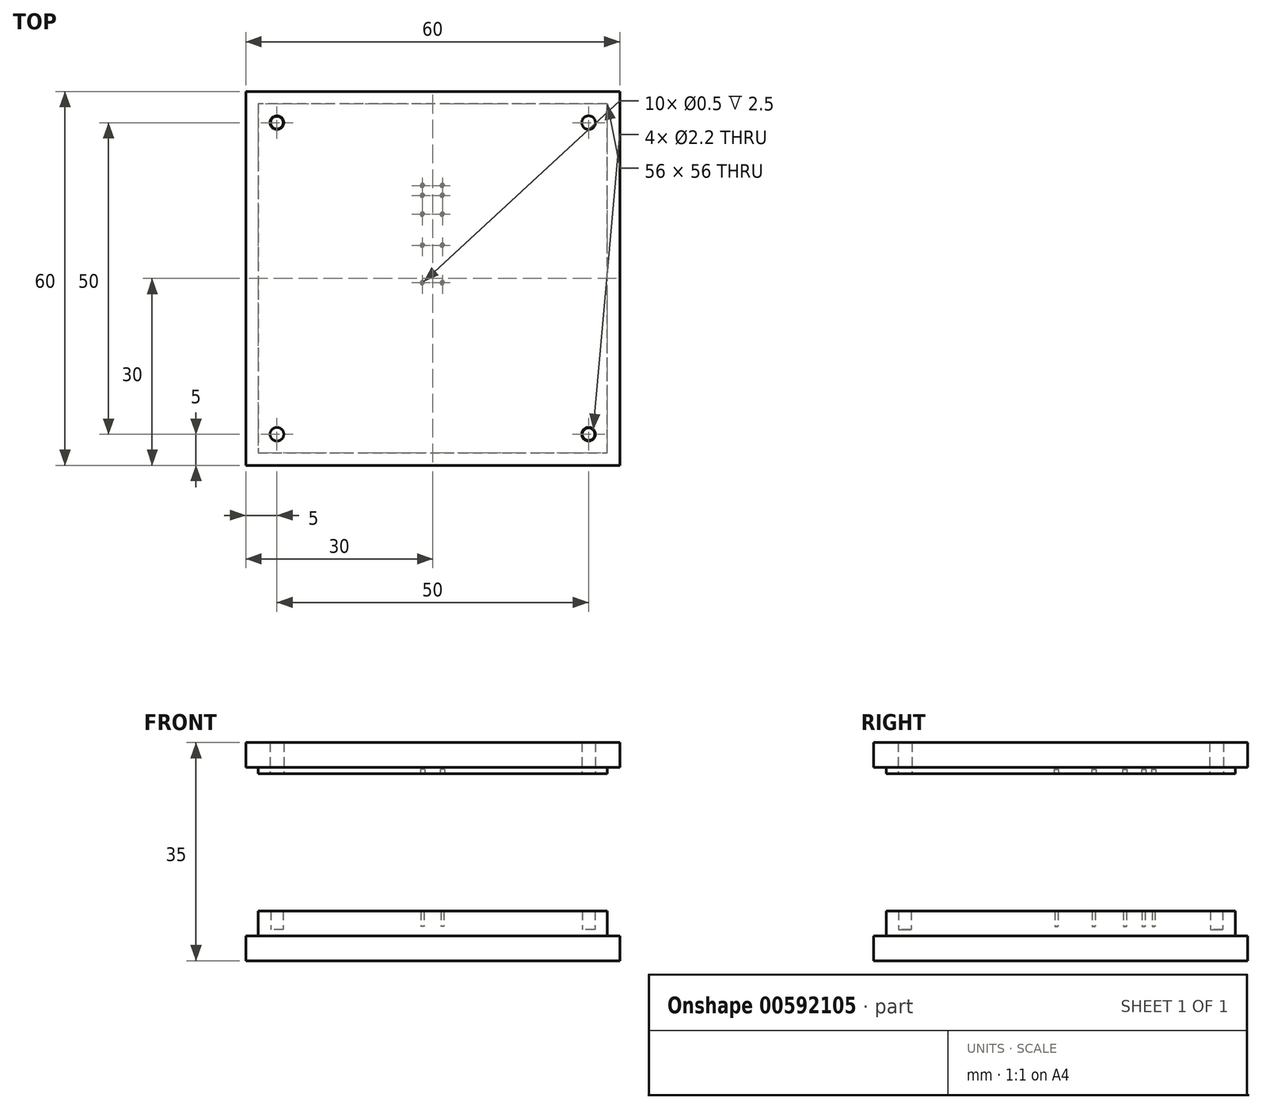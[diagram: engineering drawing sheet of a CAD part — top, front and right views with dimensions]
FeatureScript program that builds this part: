
annotation { "Feature Type Name" : "Feature", "Feature Type Description" : "" }
export const myFeature = defineFeature(function(context is Context, id is Id, definition is map)
    precondition{}
    {
        {
            var Q0;
            Q0=qCreatedBy(makeId("Top.planeOp"),FACE);
            var sketch = newSketch(context, id + "F0", { "sketchPlane" : qUnion([Q0])});
            skCircle(sketch, "E0", {"center": v(-0.48, 13.8) * mm, "radius": 0.03 * mm});
            skCircle(sketch, "E1", {"center": v(-0.48, 13.94) * mm, "radius": 0.03 * mm});
            skCircle(sketch, "E2", {"center": v(-0.48, 14.2) * mm, "radius": 0.03 * mm});
            skCircle(sketch, "E3", {"center": v(-0.13, 13.8) * mm, "radius": 0.05 * mm});
            skCircle(sketch, "E4", {"center": v(-0.13, 14) * mm, "radius": 0.05 * mm});
            skCircle(sketch, "E5", {"center": v(-0.13, 14.3) * mm, "radius": 0.05 * mm});
            skCircle(sketch, "E6", {"center": v(0.4, 13.8) * mm, "radius": 0.1 * mm});
            skCircle(sketch, "E7", {"center": v(0.4, 14.1) * mm, "radius": 0.1 * mm});
            skCircle(sketch, "E8", {"center": v(0.4, 14.5) * mm, "radius": 0.1 * mm});
            skCircle(sketch, "E9", {"center": v(-0.48, 14.5) * mm, "radius": 0.03 * mm});
            skCircle(sketch, "E10", {"center": v(-0.13, 14.6) * mm, "radius": 0.05 * mm});
            skCircle(sketch, "E11", {"center": v(-0.48, 13.8) * mm, "radius": 0.06 * mm});
            skCircle(sketch, "E12", {"center": v(-0.48, 13.94) * mm, "radius": 0.06 * mm});
            skCircle(sketch, "E13", {"center": v(-0.48, 14.2) * mm, "radius": 0.07 * mm});
            skCircle(sketch, "E14", {"center": v(-0.48, 14.5) * mm, "radius": 0.07 * mm});
            skCircle(sketch, "E15", {"center": v(-0.13, 13.8) * mm, "radius": 0.08 * mm});
            skCircle(sketch, "E16", {"center": v(-0.13, 14) * mm, "radius": 0.08 * mm});
            skCircle(sketch, "E17", {"center": v(-0.13, 14.3) * mm, "radius": 0.1 * mm});
            skCircle(sketch, "E18", {"center": v(-0.13, 14.6) * mm, "radius": 0.1 * mm});
            skCircle(sketch, "E19", {"center": v(0.4, 13.8) * mm, "radius": 0.13 * mm});
            skCircle(sketch, "E20", {"center": v(0.4, 14.1) * mm, "radius": 0.13 * mm});
            skCircle(sketch, "E21", {"center": v(0.4, 14.5) * mm, "radius": 0.15 * mm});
            skLineSegment(sketch, "E22", {"start": v(-0.25, 13.36) * mm, "end": v(-0.25, -15.14) * mm});
            skLineSegment(sketch, "E23", {"start": v(-0.21, 13.36) * mm, "end": v(-0.21, -14.64) * mm});
            skLineSegment(sketch, "E24", {"start": v(-0.17, 13.36) * mm, "end": v(-0.17, -14.14) * mm});
            skLineSegment(sketch, "E25", {"start": v(-0.13, 13.36) * mm, "end": v(-0.13, -13.64) * mm});
            skLineSegment(sketch, "E26", {"start": v(-0.09, 13.36) * mm, "end": v(-0.09, -13.14) * mm});
            skLineSegment(sketch, "E27", {"start": v(-0.05, 13.36) * mm, "end": v(-0.05, -12.64) * mm});
            skLineSegment(sketch, "E28", {"start": v(-0.01, 13.36) * mm, "end": v(-0.01, -12.14) * mm});
            skLineSegment(sketch, "E29", {"start": v(0.03, 13.36) * mm, "end": v(0.03, -11.64) * mm});
            skLineSegment(sketch, "E30", {"start": v(0.07, 13.36) * mm, "end": v(0.07, -11.14) * mm});
            skLineSegment(sketch, "E31", {"start": v(0.1, 13.36) * mm, "end": v(0.1, -10.64) * mm});
            skLineSegment(sketch, "E32", {"start": v(0.15, 13.36) * mm, "end": v(0.15, -10.14) * mm});
            skLineSegment(sketch, "E33", {"start": v(2.74, -15.44) * mm, "end": v(2.74, -15.14) * mm});
            skLineSegment(sketch, "E34", {"start": v(2.74, -15.14) * mm, "end": v(-0.26, -15.14) * mm});
            skLineSegment(sketch, "E35", {"start": v(-0.26, -15.14) * mm, "end": v(-0.26, -15.44) * mm});
            skLineSegment(sketch, "E36", {"start": v(-0.26, -15.44) * mm, "end": v(2.74, -15.44) * mm});
            skLineSegment(sketch, "E37", {"start": v(2.74, -14.94) * mm, "end": v(2.74, -14.64) * mm});
            skLineSegment(sketch, "E38", {"start": v(2.74, -14.64) * mm, "end": v(-0.22, -14.64) * mm});
            skLineSegment(sketch, "E39", {"start": v(-0.22, -14.64) * mm, "end": v(-0.22, -14.94) * mm});
            skLineSegment(sketch, "E40", {"start": v(-0.22, -14.94) * mm, "end": v(2.74, -14.94) * mm});
            skLineSegment(sketch, "E41", {"start": v(2.74, -14.44) * mm, "end": v(2.74, -14.14) * mm});
            skLineSegment(sketch, "E42", {"start": v(2.74, -14.14) * mm, "end": v(-0.18, -14.14) * mm});
            skLineSegment(sketch, "E43", {"start": v(-0.18, -14.14) * mm, "end": v(-0.18, -14.44) * mm});
            skLineSegment(sketch, "E44", {"start": v(-0.18, -14.44) * mm, "end": v(2.74, -14.44) * mm});
            skLineSegment(sketch, "E45", {"start": v(2.74, -13.94) * mm, "end": v(2.74, -13.64) * mm});
            skLineSegment(sketch, "E46", {"start": v(2.74, -13.64) * mm, "end": v(-0.14, -13.64) * mm});
            skLineSegment(sketch, "E47", {"start": v(-0.14, -13.64) * mm, "end": v(-0.14, -13.94) * mm});
            skLineSegment(sketch, "E48", {"start": v(-0.14, -13.94) * mm, "end": v(2.74, -13.94) * mm});
            skLineSegment(sketch, "E49", {"start": v(2.74, -13.44) * mm, "end": v(2.74, -13.14) * mm});
            skLineSegment(sketch, "E50", {"start": v(2.74, -13.14) * mm, "end": v(-0.1, -13.14) * mm});
            skLineSegment(sketch, "E51", {"start": v(-0.1, -13.14) * mm, "end": v(-0.1, -13.44) * mm});
            skLineSegment(sketch, "E52", {"start": v(-0.1, -13.44) * mm, "end": v(2.74, -13.44) * mm});
            skLineSegment(sketch, "E53", {"start": v(2.74, -12.94) * mm, "end": v(2.74, -12.64) * mm});
            skLineSegment(sketch, "E54", {"start": v(2.74, -12.64) * mm, "end": v(-0.06, -12.64) * mm});
            skLineSegment(sketch, "E55", {"start": v(-0.06, -12.64) * mm, "end": v(-0.06, -12.94) * mm});
            skLineSegment(sketch, "E56", {"start": v(-0.06, -12.94) * mm, "end": v(2.74, -12.94) * mm});
            skLineSegment(sketch, "E57", {"start": v(2.74, -12.44) * mm, "end": v(2.74, -12.14) * mm});
            skLineSegment(sketch, "E58", {"start": v(2.74, -12.14) * mm, "end": v(-0.02, -12.14) * mm});
            skLineSegment(sketch, "E59", {"start": v(-0.02, -12.14) * mm, "end": v(-0.02, -12.44) * mm});
            skLineSegment(sketch, "E60", {"start": v(-0.02, -12.44) * mm, "end": v(2.74, -12.44) * mm});
            skLineSegment(sketch, "E61", {"start": v(2.74, -11.94) * mm, "end": v(2.74, -11.64) * mm});
            skLineSegment(sketch, "E62", {"start": v(2.74, -11.64) * mm, "end": v(0.02, -11.64) * mm});
            skLineSegment(sketch, "E63", {"start": v(0.02, -11.64) * mm, "end": v(0.02, -11.94) * mm});
            skLineSegment(sketch, "E64", {"start": v(0.02, -11.94) * mm, "end": v(2.74, -11.94) * mm});
            skLineSegment(sketch, "E65", {"start": v(2.74, -11.44) * mm, "end": v(2.74, -11.14) * mm});
            skLineSegment(sketch, "E66", {"start": v(2.74, -11.14) * mm, "end": v(0.06, -11.14) * mm});
            skLineSegment(sketch, "E67", {"start": v(0.06, -11.14) * mm, "end": v(0.06, -11.44) * mm});
            skLineSegment(sketch, "E68", {"start": v(0.06, -11.44) * mm, "end": v(2.74, -11.44) * mm});
            skLineSegment(sketch, "E69", {"start": v(2.74, -10.94) * mm, "end": v(2.74, -10.64) * mm});
            skLineSegment(sketch, "E70", {"start": v(2.74, -10.64) * mm, "end": v(0.1, -10.64) * mm});
            skLineSegment(sketch, "E71", {"start": v(0.1, -10.64) * mm, "end": v(0.1, -10.94) * mm});
            skLineSegment(sketch, "E72", {"start": v(0.1, -10.94) * mm, "end": v(2.74, -10.94) * mm});
            skLineSegment(sketch, "E73", {"start": v(2.74, -10.44) * mm, "end": v(2.74, -10.14) * mm});
            skLineSegment(sketch, "E74", {"start": v(2.74, -10.14) * mm, "end": v(0.14, -10.14) * mm});
            skLineSegment(sketch, "E75", {"start": v(0.14, -10.14) * mm, "end": v(0.14, -10.44) * mm});
            skLineSegment(sketch, "E76", {"start": v(0.14, -10.44) * mm, "end": v(2.74, -10.44) * mm});
            skLineSegment(sketch, "E77", {"start": v(-0.29, 13.74) * mm, "end": v(-0.29, 13.84) * mm});
            skLineSegment(sketch, "E78", {"start": v(-0.25, 13.74) * mm, "end": v(-0.25, 13.84) * mm});
            skLineSegment(sketch, "E79", {"start": v(-0.29, 13.84) * mm, "end": v(-0.29, 13.92) * mm});
            skLineSegment(sketch, "E80", {"start": v(-0.29, 13.92) * mm, "end": v(-0.33, 14) * mm});
            skLineSegment(sketch, "E81", {"start": v(-0.33, 14) * mm, "end": v(-0.33, 14.04) * mm});
            skLineSegment(sketch, "E82", {"start": v(-0.25, 13.84) * mm, "end": v(-0.25, 13.95) * mm});
            skLineSegment(sketch, "E83", {"start": v(-0.25, 13.95) * mm, "end": v(-0.3, 14.02) * mm});
            skLineSegment(sketch, "E84", {"start": v(-0.3, 14.02) * mm, "end": v(-0.3, 14.16) * mm});
            skLineSegment(sketch, "E85", {"start": v(-0.3, 14.16) * mm, "end": v(-0.3, 14.3) * mm});
            skLineSegment(sketch, "E86", {"start": v(-0.3, 14.3) * mm, "end": v(-0.48, 14.5) * mm});
            skLineSegment(sketch, "E87", {"start": v(-0.25, 13.74) * mm, "end": v(-0.25, 13.62) * mm});
            skLineSegment(sketch, "E88", {"start": v(-0.25, 13.62) * mm, "end": v(-0.13, 13.5) * mm});
            skLineSegment(sketch, "E89", {"start": v(-0.13, 13.5) * mm, "end": v(-0.13, 13.36) * mm});
            skLineSegment(sketch, "E90", {"start": v(-0.29, 13.74) * mm, "end": v(-0.29, 13.6) * mm});
            skLineSegment(sketch, "E91", {"start": v(-0.29, 13.6) * mm, "end": v(-0.17, 13.48) * mm});
            skLineSegment(sketch, "E92", {"start": v(-0.17, 13.48) * mm, "end": v(-0.17, 13.36) * mm});
            skLineSegment(sketch, "E93", {"start": v(-0.33, 13.74) * mm, "end": v(-0.33, 13.56) * mm});
            skLineSegment(sketch, "E94", {"start": v(-0.33, 13.56) * mm, "end": v(-0.21, 13.44) * mm});
            skLineSegment(sketch, "E95", {"start": v(-0.21, 13.44) * mm, "end": v(-0.21, 13.36) * mm});
            skLineSegment(sketch, "E96", {"start": v(-0.48, 13.8) * mm, "end": v(-0.37, 13.68) * mm});
            skLineSegment(sketch, "E97", {"start": v(-0.37, 13.68) * mm, "end": v(-0.37, 13.54) * mm});
            skLineSegment(sketch, "E98", {"start": v(-0.37, 13.54) * mm, "end": v(-0.25, 13.42) * mm});
            skLineSegment(sketch, "E99", {"start": v(-0.25, 13.42) * mm, "end": v(-0.25, 13.36) * mm});
            skLineSegment(sketch, "E100", {"start": v(0, 13.7) * mm, "end": v(0, 13.82) * mm});
            skLineSegment(sketch, "E101", {"start": v(0.05, 13.7) * mm, "end": v(0.05, 14.07) * mm});
            skLineSegment(sketch, "E102", {"start": v(0.09, 13.7) * mm, "end": v(0.09, 14.07) * mm});
            skLineSegment(sketch, "E103", {"start": v(0.13, 13.7) * mm, "end": v(0.13, 14.07) * mm});
            skLineSegment(sketch, "E104", {"start": v(-0.13, 14.6) * mm, "end": v(0.09, 14.38) * mm});
            skLineSegment(sketch, "E105", {"start": v(0.09, 14.38) * mm, "end": v(0.09, 14.07) * mm});
            skLineSegment(sketch, "E106", {"start": v(-0.13, 14.3) * mm, "end": v(0.05, 14.12) * mm});
            skLineSegment(sketch, "E107", {"start": v(0.05, 14.12) * mm, "end": v(0.05, 14.07) * mm});
            skLineSegment(sketch, "E108", {"start": v(0.35, 14.5) * mm, "end": v(0.13, 14.27) * mm});
            skLineSegment(sketch, "E109", {"start": v(0.13, 14.27) * mm, "end": v(0.13, 14.07) * mm});
            skLineSegment(sketch, "E110", {"start": v(0.35, 14.1) * mm, "end": v(0.17, 13.9) * mm});
            skLineSegment(sketch, "E111", {"start": v(0.17, 13.9) * mm, "end": v(0.17, 13.83) * mm});
            skLineSegment(sketch, "E112", {"start": v(-0.13, 14) * mm, "end": v(0, 13.86) * mm});
            skLineSegment(sketch, "E113", {"start": v(0, 13.86) * mm, "end": v(0, 13.82) * mm});
            skLineSegment(sketch, "E114", {"start": v(-0.09, 13.36) * mm, "end": v(-0.09, 13.64) * mm});
            skLineSegment(sketch, "E115", {"start": v(-0.09, 13.64) * mm, "end": v(-0.12, 13.68) * mm});
            skLineSegment(sketch, "E116", {"start": v(-0.12, 13.68) * mm, "end": v(-0.13, 13.8) * mm});
            skLineSegment(sketch, "E117", {"start": v(-0.05, 13.36) * mm, "end": v(-0.05, 13.56) * mm});
            skLineSegment(sketch, "E118", {"start": v(-0.05, 13.56) * mm, "end": v(0, 13.62) * mm});
            skLineSegment(sketch, "E119", {"start": v(0, 13.62) * mm, "end": v(0, 13.7) * mm});
            skLineSegment(sketch, "E120", {"start": v(-0.01, 13.36) * mm, "end": v(-0.01, 13.52) * mm});
            skLineSegment(sketch, "E121", {"start": v(-0.01, 13.52) * mm, "end": v(0.05, 13.57) * mm});
            skLineSegment(sketch, "E122", {"start": v(0.05, 13.57) * mm, "end": v(0.05, 13.7) * mm});
            skLineSegment(sketch, "E123", {"start": v(0.03, 13.36) * mm, "end": v(0.03, 13.48) * mm});
            skLineSegment(sketch, "E124", {"start": v(0.03, 13.48) * mm, "end": v(0.09, 13.54) * mm});
            skLineSegment(sketch, "E125", {"start": v(0.09, 13.54) * mm, "end": v(0.09, 13.7) * mm});
            skLineSegment(sketch, "E126", {"start": v(0.07, 13.36) * mm, "end": v(0.07, 13.44) * mm});
            skLineSegment(sketch, "E127", {"start": v(0.07, 13.44) * mm, "end": v(0.13, 13.5) * mm});
            skLineSegment(sketch, "E128", {"start": v(0.13, 13.5) * mm, "end": v(0.13, 13.7) * mm});
            skLineSegment(sketch, "E129", {"start": v(0.1, 13.36) * mm, "end": v(0.1, 13.4) * mm});
            skLineSegment(sketch, "E130", {"start": v(0.1, 13.4) * mm, "end": v(0.17, 13.46) * mm});
            skLineSegment(sketch, "E131", {"start": v(0.17, 13.46) * mm, "end": v(0.17, 13.83) * mm});
            skLineSegment(sketch, "E132", {"start": v(0.15, 13.36) * mm, "end": v(0.15, 13.37) * mm});
            skLineSegment(sketch, "E133", {"start": v(0.15, 13.36) * mm, "end": v(0.15, 13.38) * mm});
            skLineSegment(sketch, "E134", {"start": v(0.15, 13.38) * mm, "end": v(0.2, 13.44) * mm});
            skLineSegment(sketch, "E135", {"start": v(0.2, 13.44) * mm, "end": v(0.2, 13.56) * mm});
            skLineSegment(sketch, "E136", {"start": v(0.35, 13.8) * mm, "end": v(0.2, 13.65) * mm});
            skLineSegment(sketch, "E137", {"start": v(0.2, 13.65) * mm, "end": v(0.2, 13.56) * mm});
            skLineSegment(sketch, "E138", {"start": v(-0.48, 13.94) * mm, "end": v(-0.33, 13.8) * mm});
            skLineSegment(sketch, "E139", {"start": v(-0.33, 13.8) * mm, "end": v(-0.33, 13.74) * mm});
            skLineSegment(sketch, "E140", {"start": v(-0.48, 14.2) * mm, "end": v(-0.33, 14.07) * mm});
            skLineSegment(sketch, "E141", {"start": v(-0.33, 14.07) * mm, "end": v(-0.33, 14.04) * mm});
            skLineSegment(sketch, "E142", {"start": v(-2.94, -15.8) * mm, "end": v(2.84, -15.8) * mm});
            skLineSegment(sketch, "E143", {"start": v(2.84, -15.8) * mm, "end": v(2.84, 15.8) * mm});
            skLineSegment(sketch, "E144", {"start": v(2.84, 15.8) * mm, "end": v(-2.94, 15.8) * mm});
            skLineSegment(sketch, "E145", {"start": v(-2.94, 15.8) * mm, "end": v(-2.94, -15.8) * mm});
            skLineSegment(sketch, "E146", {"start": v(2.25, 12.8) * mm, "end": v(2.25, 13.2) * mm});
            skLineSegment(sketch, "E147", {"start": v(2.05, 13) * mm, "end": v(2.45, 13) * mm});
            skCircle(sketch, "E148", {"center": v(1.55, 13.3) * mm, "radius": 0.25 * mm});
            skCircle(sketch, "E149", {"center": v(1.55, 13.3) * mm, "radius": 0.2 * mm});
            skCircle(sketch, "E150", {"center": v(1.55, 13.3) * mm, "radius": 0.3 * mm});
            skCircle(sketch, "E151", {"center": v(1.55, 13.3) * mm, "radius": 0.35 * mm});
            skCircle(sketch, "E152", {"center": v(1.55, 14.9) * mm, "radius": 0.25 * mm});
            skCircle(sketch, "E153", {"center": v(1.55, 14.9) * mm, "radius": 0.2 * mm});
            skCircle(sketch, "E154", {"center": v(1.55, 14.9) * mm, "radius": 0.3 * mm});
            skCircle(sketch, "E155", {"center": v(1.55, 14.9) * mm, "radius": 0.35 * mm});
            skLineSegment(sketch, "E156", {"start": v(0.85, 15.4) * mm, "end": v(0.85, 15) * mm});
            skLineSegment(sketch, "E157", {"start": v(0.65, 15.2) * mm, "end": v(1.05, 15.2) * mm});
            skLineSegment(sketch, "E158", {"start": v(0.85, 12.8) * mm, "end": v(0.85, 13.2) * mm});
            skLineSegment(sketch, "E159", {"start": v(0.65, 13) * mm, "end": v(1.05, 13) * mm});
            skLineSegment(sketch, "E160", {"start": v(-2.35, 15.4) * mm, "end": v(-2.35, 15) * mm});
            skLineSegment(sketch, "E161", {"start": v(-2.15, 15.2) * mm, "end": v(-2.55, 15.2) * mm});
            skCircle(sketch, "E162", {"center": v(-1.65, 13.3) * mm, "radius": 0.25 * mm});
            skCircle(sketch, "E163", {"center": v(-1.65, 13.3) * mm, "radius": 0.2 * mm});
            skCircle(sketch, "E164", {"center": v(-1.65, 13.3) * mm, "radius": 0.3 * mm});
            skCircle(sketch, "E165", {"center": v(-1.65, 13.3) * mm, "radius": 0.35 * mm});
            skCircle(sketch, "E166", {"center": v(-1.65, 14.9) * mm, "radius": 0.25 * mm});
            skCircle(sketch, "E167", {"center": v(-1.65, 14.9) * mm, "radius": 0.2 * mm});
            skCircle(sketch, "E168", {"center": v(-1.65, 14.9) * mm, "radius": 0.3 * mm});
            skCircle(sketch, "E169", {"center": v(-1.65, 14.9) * mm, "radius": 0.35 * mm});
            skLineSegment(sketch, "E170", {"start": v(-0.95, 15.4) * mm, "end": v(-0.95, 15) * mm});
            skLineSegment(sketch, "E171", {"start": v(-0.75, 15.2) * mm, "end": v(-1.15, 15.2) * mm});
            skLineSegment(sketch, "E172", {"start": v(-0.95, 12.8) * mm, "end": v(-0.95, 13.2) * mm});
            skLineSegment(sketch, "E173", {"start": v(-0.75, 13) * mm, "end": v(-1.15, 13) * mm});
            skLineSegment(sketch, "E174", {"start": v(1.18, 14.07) * mm, "end": v(1.35, 14.07) * mm});
            skLineSegment(sketch, "E175", {"start": v(1.35, 14.07) * mm, "end": v(1.35, 14.12) * mm});
            skLineSegment(sketch, "E176", {"start": v(1.35, 14.12) * mm, "end": v(1.18, 14.12) * mm});
            skLineSegment(sketch, "E177", {"start": v(1.13, 14.12) * mm, "end": v(0.95, 14.12) * mm});
            skLineSegment(sketch, "E178", {"start": v(0.95, 14.12) * mm, "end": v(0.95, 14.07) * mm});
            skLineSegment(sketch, "E179", {"start": v(0.95, 14.07) * mm, "end": v(1.13, 14.07) * mm});
            skLineSegment(sketch, "E180", {"start": v(1.18, 14.12) * mm, "end": v(1.18, 14.3) * mm});
            skLineSegment(sketch, "E181", {"start": v(1.18, 14.3) * mm, "end": v(1.13, 14.3) * mm});
            skLineSegment(sketch, "E182", {"start": v(1.13, 14.3) * mm, "end": v(1.13, 14.12) * mm});
            skLineSegment(sketch, "E183", {"start": v(1.13, 14.07) * mm, "end": v(1.13, 13.9) * mm});
            skLineSegment(sketch, "E184", {"start": v(1.13, 13.9) * mm, "end": v(1.18, 13.9) * mm});
            skLineSegment(sketch, "E185", {"start": v(1.18, 13.9) * mm, "end": v(1.18, 14.07) * mm});
            skLineSegment(sketch, "E186", {"start": v(1.32, 14.24) * mm, "end": v(1.39, 14.24) * mm});
            skLineSegment(sketch, "E187", {"start": v(1.39, 14.24) * mm, "end": v(1.39, 14.26) * mm});
            skLineSegment(sketch, "E188", {"start": v(1.39, 14.26) * mm, "end": v(1.32, 14.26) * mm});
            skLineSegment(sketch, "E189", {"start": v(1.3, 14.26) * mm, "end": v(1.23, 14.26) * mm});
            skLineSegment(sketch, "E190", {"start": v(1.23, 14.26) * mm, "end": v(1.23, 14.24) * mm});
            skLineSegment(sketch, "E191", {"start": v(1.23, 14.24) * mm, "end": v(1.3, 14.24) * mm});
            skLineSegment(sketch, "E192", {"start": v(1.32, 14.26) * mm, "end": v(1.32, 14.33) * mm});
            skLineSegment(sketch, "E193", {"start": v(1.32, 14.33) * mm, "end": v(1.3, 14.33) * mm});
            skLineSegment(sketch, "E194", {"start": v(1.3, 14.33) * mm, "end": v(1.3, 14.26) * mm});
            skLineSegment(sketch, "E195", {"start": v(1.3, 14.24) * mm, "end": v(1.3, 14.17) * mm});
            skLineSegment(sketch, "E196", {"start": v(1.3, 14.17) * mm, "end": v(1.32, 14.17) * mm});
            skLineSegment(sketch, "E197", {"start": v(1.32, 14.17) * mm, "end": v(1.32, 14.24) * mm});
            skLineSegment(sketch, "E198", {"start": v(1.32, 13.94) * mm, "end": v(1.39, 13.94) * mm});
            skLineSegment(sketch, "E199", {"start": v(1.39, 13.94) * mm, "end": v(1.39, 13.92) * mm});
            skLineSegment(sketch, "E200", {"start": v(1.39, 13.92) * mm, "end": v(1.32, 13.92) * mm});
            skLineSegment(sketch, "E201", {"start": v(1.3, 13.92) * mm, "end": v(1.23, 13.92) * mm});
            skLineSegment(sketch, "E202", {"start": v(1.23, 13.92) * mm, "end": v(1.23, 13.94) * mm});
            skLineSegment(sketch, "E203", {"start": v(1.23, 13.94) * mm, "end": v(1.3, 13.94) * mm});
            skLineSegment(sketch, "E204", {"start": v(1.32, 13.92) * mm, "end": v(1.32, 13.85) * mm});
            skLineSegment(sketch, "E205", {"start": v(1.32, 13.85) * mm, "end": v(1.3, 13.85) * mm});
            skLineSegment(sketch, "E206", {"start": v(1.3, 13.85) * mm, "end": v(1.3, 13.92) * mm});
            skLineSegment(sketch, "E207", {"start": v(1.3, 13.94) * mm, "end": v(1.3, 14.01) * mm});
            skLineSegment(sketch, "E208", {"start": v(1.3, 14.01) * mm, "end": v(1.32, 14.01) * mm});
            skLineSegment(sketch, "E209", {"start": v(1.32, 14.01) * mm, "end": v(1.32, 13.94) * mm});
            skLineSegment(sketch, "E210", {"start": v(0.98, 14.24) * mm, "end": v(0.9, 14.24) * mm});
            skLineSegment(sketch, "E211", {"start": v(0.9, 14.24) * mm, "end": v(0.9, 14.26) * mm});
            skLineSegment(sketch, "E212", {"start": v(0.9, 14.26) * mm, "end": v(0.98, 14.26) * mm});
            skLineSegment(sketch, "E213", {"start": v(1, 14.26) * mm, "end": v(1.07, 14.26) * mm});
            skLineSegment(sketch, "E214", {"start": v(1.07, 14.26) * mm, "end": v(1.07, 14.24) * mm});
            skLineSegment(sketch, "E215", {"start": v(1.07, 14.24) * mm, "end": v(1, 14.24) * mm});
            skLineSegment(sketch, "E216", {"start": v(0.98, 14.26) * mm, "end": v(0.98, 14.33) * mm});
            skLineSegment(sketch, "E217", {"start": v(0.98, 14.33) * mm, "end": v(1, 14.33) * mm});
            skLineSegment(sketch, "E218", {"start": v(1, 14.33) * mm, "end": v(1, 14.26) * mm});
            skLineSegment(sketch, "E219", {"start": v(1, 14.24) * mm, "end": v(1, 14.17) * mm});
            skLineSegment(sketch, "E220", {"start": v(1, 14.17) * mm, "end": v(0.98, 14.17) * mm});
            skLineSegment(sketch, "E221", {"start": v(0.98, 14.17) * mm, "end": v(0.98, 14.24) * mm});
            skLineSegment(sketch, "E222", {"start": v(0.98, 13.94) * mm, "end": v(0.9, 13.94) * mm});
            skLineSegment(sketch, "E223", {"start": v(0.9, 13.94) * mm, "end": v(0.9, 13.92) * mm});
            skLineSegment(sketch, "E224", {"start": v(0.9, 13.92) * mm, "end": v(0.98, 13.92) * mm});
            skLineSegment(sketch, "E225", {"start": v(1, 13.92) * mm, "end": v(1.07, 13.92) * mm});
            skLineSegment(sketch, "E226", {"start": v(1.07, 13.92) * mm, "end": v(1.07, 13.94) * mm});
            skLineSegment(sketch, "E227", {"start": v(1.07, 13.94) * mm, "end": v(1, 13.94) * mm});
            skLineSegment(sketch, "E228", {"start": v(0.98, 13.92) * mm, "end": v(0.98, 13.85) * mm});
            skLineSegment(sketch, "E229", {"start": v(0.98, 13.85) * mm, "end": v(1, 13.85) * mm});
            skLineSegment(sketch, "E230", {"start": v(1, 13.85) * mm, "end": v(1, 13.92) * mm});
            skLineSegment(sketch, "E231", {"start": v(1, 13.94) * mm, "end": v(1, 14.01) * mm});
            skLineSegment(sketch, "E232", {"start": v(1, 14.01) * mm, "end": v(0.98, 14.01) * mm});
            skLineSegment(sketch, "E233", {"start": v(0.98, 14.01) * mm, "end": v(0.98, 13.94) * mm});
            skLineSegment(sketch, "E234", {"start": v(-1.28, 14.07) * mm, "end": v(-1.45, 14.07) * mm});
            skLineSegment(sketch, "E235", {"start": v(-1.45, 14.07) * mm, "end": v(-1.45, 14.12) * mm});
            skLineSegment(sketch, "E236", {"start": v(-1.45, 14.12) * mm, "end": v(-1.28, 14.12) * mm});
            skLineSegment(sketch, "E237", {"start": v(-1.23, 14.12) * mm, "end": v(-1.05, 14.12) * mm});
            skLineSegment(sketch, "E238", {"start": v(-1.05, 14.12) * mm, "end": v(-1.05, 14.07) * mm});
            skLineSegment(sketch, "E239", {"start": v(-1.05, 14.07) * mm, "end": v(-1.23, 14.07) * mm});
            skLineSegment(sketch, "E240", {"start": v(-1.28, 14.12) * mm, "end": v(-1.28, 14.3) * mm});
            skLineSegment(sketch, "E241", {"start": v(-1.28, 14.3) * mm, "end": v(-1.23, 14.3) * mm});
            skLineSegment(sketch, "E242", {"start": v(-1.23, 14.3) * mm, "end": v(-1.23, 14.12) * mm});
            skLineSegment(sketch, "E243", {"start": v(-1.23, 14.07) * mm, "end": v(-1.23, 13.9) * mm});
            skLineSegment(sketch, "E244", {"start": v(-1.23, 13.9) * mm, "end": v(-1.28, 13.9) * mm});
            skLineSegment(sketch, "E245", {"start": v(-1.28, 13.9) * mm, "end": v(-1.28, 14.07) * mm});
            skLineSegment(sketch, "E246", {"start": v(-1.42, 14.24) * mm, "end": v(-1.49, 14.24) * mm});
            skLineSegment(sketch, "E247", {"start": v(-1.49, 14.24) * mm, "end": v(-1.49, 14.26) * mm});
            skLineSegment(sketch, "E248", {"start": v(-1.49, 14.26) * mm, "end": v(-1.42, 14.26) * mm});
            skLineSegment(sketch, "E249", {"start": v(-1.4, 14.26) * mm, "end": v(-1.33, 14.26) * mm});
            skLineSegment(sketch, "E250", {"start": v(-1.33, 14.26) * mm, "end": v(-1.33, 14.24) * mm});
            skLineSegment(sketch, "E251", {"start": v(-1.33, 14.24) * mm, "end": v(-1.4, 14.24) * mm});
            skLineSegment(sketch, "E252", {"start": v(-1.42, 14.26) * mm, "end": v(-1.42, 14.33) * mm});
            skLineSegment(sketch, "E253", {"start": v(-1.42, 14.33) * mm, "end": v(-1.4, 14.33) * mm});
            skLineSegment(sketch, "E254", {"start": v(-1.4, 14.33) * mm, "end": v(-1.4, 14.26) * mm});
            skLineSegment(sketch, "E255", {"start": v(-1.4, 14.24) * mm, "end": v(-1.4, 14.17) * mm});
            skLineSegment(sketch, "E256", {"start": v(-1.4, 14.17) * mm, "end": v(-1.42, 14.17) * mm});
            skLineSegment(sketch, "E257", {"start": v(-1.42, 14.17) * mm, "end": v(-1.42, 14.24) * mm});
            skLineSegment(sketch, "E258", {"start": v(-1.42, 13.94) * mm, "end": v(-1.49, 13.94) * mm});
            skLineSegment(sketch, "E259", {"start": v(-1.49, 13.94) * mm, "end": v(-1.49, 13.92) * mm});
            skLineSegment(sketch, "E260", {"start": v(-1.49, 13.92) * mm, "end": v(-1.42, 13.92) * mm});
            skLineSegment(sketch, "E261", {"start": v(-1.4, 13.92) * mm, "end": v(-1.33, 13.92) * mm});
            skLineSegment(sketch, "E262", {"start": v(-1.33, 13.92) * mm, "end": v(-1.33, 13.94) * mm});
            skLineSegment(sketch, "E263", {"start": v(-1.33, 13.94) * mm, "end": v(-1.4, 13.94) * mm});
            skLineSegment(sketch, "E264", {"start": v(-1.42, 13.92) * mm, "end": v(-1.42, 13.85) * mm});
            skLineSegment(sketch, "E265", {"start": v(-1.42, 13.85) * mm, "end": v(-1.4, 13.85) * mm});
            skLineSegment(sketch, "E266", {"start": v(-1.4, 13.85) * mm, "end": v(-1.4, 13.92) * mm});
            skLineSegment(sketch, "E267", {"start": v(-1.4, 13.94) * mm, "end": v(-1.4, 14.01) * mm});
            skLineSegment(sketch, "E268", {"start": v(-1.4, 14.01) * mm, "end": v(-1.42, 14.01) * mm});
            skLineSegment(sketch, "E269", {"start": v(-1.42, 14.01) * mm, "end": v(-1.42, 13.94) * mm});
            skLineSegment(sketch, "E270", {"start": v(-1.08, 14.24) * mm, "end": v(-1.01, 14.24) * mm});
            skLineSegment(sketch, "E271", {"start": v(-1.01, 14.24) * mm, "end": v(-1.01, 14.26) * mm});
            skLineSegment(sketch, "E272", {"start": v(-1.01, 14.26) * mm, "end": v(-1.08, 14.26) * mm});
            skLineSegment(sketch, "E273", {"start": v(-1.1, 14.26) * mm, "end": v(-1.17, 14.26) * mm});
            skLineSegment(sketch, "E274", {"start": v(-1.17, 14.26) * mm, "end": v(-1.17, 14.24) * mm});
            skLineSegment(sketch, "E275", {"start": v(-1.17, 14.24) * mm, "end": v(-1.1, 14.24) * mm});
            skLineSegment(sketch, "E276", {"start": v(-1.08, 14.26) * mm, "end": v(-1.08, 14.33) * mm});
            skLineSegment(sketch, "E277", {"start": v(-1.08, 14.33) * mm, "end": v(-1.1, 14.33) * mm});
            skLineSegment(sketch, "E278", {"start": v(-1.1, 14.33) * mm, "end": v(-1.1, 14.26) * mm});
            skLineSegment(sketch, "E279", {"start": v(-1.1, 14.24) * mm, "end": v(-1.1, 14.17) * mm});
            skLineSegment(sketch, "E280", {"start": v(-1.1, 14.17) * mm, "end": v(-1.08, 14.17) * mm});
            skLineSegment(sketch, "E281", {"start": v(-1.08, 14.17) * mm, "end": v(-1.08, 14.24) * mm});
            skLineSegment(sketch, "E282", {"start": v(-1.08, 13.94) * mm, "end": v(-1.01, 13.94) * mm});
            skLineSegment(sketch, "E283", {"start": v(-1.01, 13.94) * mm, "end": v(-1.01, 13.92) * mm});
            skLineSegment(sketch, "E284", {"start": v(-1.01, 13.92) * mm, "end": v(-1.08, 13.92) * mm});
            skLineSegment(sketch, "E285", {"start": v(-1.1, 13.92) * mm, "end": v(-1.17, 13.92) * mm});
            skLineSegment(sketch, "E286", {"start": v(-1.17, 13.92) * mm, "end": v(-1.17, 13.94) * mm});
            skLineSegment(sketch, "E287", {"start": v(-1.17, 13.94) * mm, "end": v(-1.1, 13.94) * mm});
            skLineSegment(sketch, "E288", {"start": v(-1.08, 13.92) * mm, "end": v(-1.08, 13.85) * mm});
            skLineSegment(sketch, "E289", {"start": v(-1.08, 13.85) * mm, "end": v(-1.1, 13.85) * mm});
            skLineSegment(sketch, "E290", {"start": v(-1.1, 13.85) * mm, "end": v(-1.1, 13.92) * mm});
            skLineSegment(sketch, "E291", {"start": v(-1.1, 13.94) * mm, "end": v(-1.1, 14.01) * mm});
            skLineSegment(sketch, "E292", {"start": v(-1.1, 14.01) * mm, "end": v(-1.08, 14.01) * mm});
            skLineSegment(sketch, "E293", {"start": v(-1.08, 14.01) * mm, "end": v(-1.08, 13.94) * mm});
            skLineSegment(sketch, "E294", {"start": v(-0.03, 15.27) * mm, "end": v(0.15, 15.27) * mm});
            skLineSegment(sketch, "E295", {"start": v(0.15, 15.27) * mm, "end": v(0.15, 15.32) * mm});
            skLineSegment(sketch, "E296", {"start": v(0.15, 15.32) * mm, "end": v(-0.03, 15.32) * mm});
            skLineSegment(sketch, "E297", {"start": v(-0.08, 15.32) * mm, "end": v(-0.25, 15.32) * mm});
            skLineSegment(sketch, "E298", {"start": v(-0.25, 15.32) * mm, "end": v(-0.25, 15.27) * mm});
            skLineSegment(sketch, "E299", {"start": v(-0.25, 15.27) * mm, "end": v(-0.08, 15.27) * mm});
            skLineSegment(sketch, "E300", {"start": v(-0.03, 15.32) * mm, "end": v(-0.03, 15.5) * mm});
            skLineSegment(sketch, "E301", {"start": v(-0.03, 15.5) * mm, "end": v(-0.08, 15.5) * mm});
            skLineSegment(sketch, "E302", {"start": v(-0.08, 15.5) * mm, "end": v(-0.08, 15.32) * mm});
            skLineSegment(sketch, "E303", {"start": v(-0.08, 15.27) * mm, "end": v(-0.08, 15.1) * mm});
            skLineSegment(sketch, "E304", {"start": v(-0.08, 15.1) * mm, "end": v(-0.02, 15.1) * mm});
            skLineSegment(sketch, "E305", {"start": v(-0.03, 15.1) * mm, "end": v(-0.03, 15.27) * mm});
            skLineSegment(sketch, "E306", {"start": v(0.12, 15.44) * mm, "end": v(0.19, 15.44) * mm});
            skLineSegment(sketch, "E307", {"start": v(0.19, 15.44) * mm, "end": v(0.19, 15.46) * mm});
            skLineSegment(sketch, "E308", {"start": v(0.19, 15.46) * mm, "end": v(0.12, 15.46) * mm});
            skLineSegment(sketch, "E309", {"start": v(0.1, 15.46) * mm, "end": v(0.03, 15.46) * mm});
            skLineSegment(sketch, "E310", {"start": v(0.03, 15.46) * mm, "end": v(0.03, 15.44) * mm});
            skLineSegment(sketch, "E311", {"start": v(0.03, 15.44) * mm, "end": v(0.1, 15.44) * mm});
            skLineSegment(sketch, "E312", {"start": v(0.12, 15.46) * mm, "end": v(0.12, 15.53) * mm});
            skLineSegment(sketch, "E313", {"start": v(0.12, 15.53) * mm, "end": v(0.1, 15.53) * mm});
            skLineSegment(sketch, "E314", {"start": v(0.1, 15.53) * mm, "end": v(0.1, 15.46) * mm});
            skLineSegment(sketch, "E315", {"start": v(0.1, 15.44) * mm, "end": v(0.1, 15.37) * mm});
            skLineSegment(sketch, "E316", {"start": v(0.1, 15.37) * mm, "end": v(0.12, 15.37) * mm});
            skLineSegment(sketch, "E317", {"start": v(0.12, 15.37) * mm, "end": v(0.12, 15.44) * mm});
            skLineSegment(sketch, "E318", {"start": v(0.12, 15.14) * mm, "end": v(0.19, 15.14) * mm});
            skLineSegment(sketch, "E319", {"start": v(0.19, 15.14) * mm, "end": v(0.19, 15.12) * mm});
            skLineSegment(sketch, "E320", {"start": v(0.19, 15.12) * mm, "end": v(0.12, 15.12) * mm});
            skLineSegment(sketch, "E321", {"start": v(0.1, 15.12) * mm, "end": v(0.03, 15.12) * mm});
            skLineSegment(sketch, "E322", {"start": v(0.03, 15.12) * mm, "end": v(0.03, 15.14) * mm});
            skLineSegment(sketch, "E323", {"start": v(0.03, 15.14) * mm, "end": v(0.1, 15.14) * mm});
            skLineSegment(sketch, "E324", {"start": v(0.12, 15.12) * mm, "end": v(0.12, 15.05) * mm});
            skLineSegment(sketch, "E325", {"start": v(0.12, 15.05) * mm, "end": v(0.1, 15.05) * mm});
            skLineSegment(sketch, "E326", {"start": v(0.1, 15.05) * mm, "end": v(0.1, 15.12) * mm});
            skLineSegment(sketch, "E327", {"start": v(0.1, 15.14) * mm, "end": v(0.1, 15.21) * mm});
            skLineSegment(sketch, "E328", {"start": v(0.1, 15.21) * mm, "end": v(0.12, 15.21) * mm});
            skLineSegment(sketch, "E329", {"start": v(0.12, 15.21) * mm, "end": v(0.12, 15.14) * mm});
            skLineSegment(sketch, "E330", {"start": v(-0.22, 15.44) * mm, "end": v(-0.29, 15.44) * mm});
            skLineSegment(sketch, "E331", {"start": v(-0.29, 15.44) * mm, "end": v(-0.29, 15.46) * mm});
            skLineSegment(sketch, "E332", {"start": v(-0.29, 15.46) * mm, "end": v(-0.22, 15.46) * mm});
            skLineSegment(sketch, "E333", {"start": v(-0.2, 15.46) * mm, "end": v(-0.13, 15.46) * mm});
            skLineSegment(sketch, "E334", {"start": v(-0.13, 15.46) * mm, "end": v(-0.13, 15.44) * mm});
            skLineSegment(sketch, "E335", {"start": v(-0.13, 15.44) * mm, "end": v(-0.2, 15.44) * mm});
            skLineSegment(sketch, "E336", {"start": v(-0.22, 15.46) * mm, "end": v(-0.22, 15.53) * mm});
            skLineSegment(sketch, "E337", {"start": v(-0.22, 15.53) * mm, "end": v(-0.2, 15.53) * mm});
            skLineSegment(sketch, "E338", {"start": v(-0.2, 15.53) * mm, "end": v(-0.2, 15.46) * mm});
            skLineSegment(sketch, "E339", {"start": v(-0.2, 15.44) * mm, "end": v(-0.2, 15.37) * mm});
            skLineSegment(sketch, "E340", {"start": v(-0.2, 15.37) * mm, "end": v(-0.22, 15.37) * mm});
            skLineSegment(sketch, "E341", {"start": v(-0.22, 15.37) * mm, "end": v(-0.22, 15.44) * mm});
            skLineSegment(sketch, "E342", {"start": v(-0.22, 15.14) * mm, "end": v(-0.29, 15.14) * mm});
            skLineSegment(sketch, "E343", {"start": v(-0.29, 15.14) * mm, "end": v(-0.29, 15.12) * mm});
            skLineSegment(sketch, "E344", {"start": v(-0.29, 15.12) * mm, "end": v(-0.22, 15.12) * mm});
            skLineSegment(sketch, "E345", {"start": v(-0.2, 15.12) * mm, "end": v(-0.13, 15.12) * mm});
            skLineSegment(sketch, "E346", {"start": v(-0.13, 15.12) * mm, "end": v(-0.13, 15.14) * mm});
            skLineSegment(sketch, "E347", {"start": v(-0.13, 15.14) * mm, "end": v(-0.2, 15.14) * mm});
            skLineSegment(sketch, "E348", {"start": v(-0.22, 15.12) * mm, "end": v(-0.22, 15.05) * mm});
            skLineSegment(sketch, "E349", {"start": v(-0.22, 15.05) * mm, "end": v(-0.2, 15.05) * mm});
            skLineSegment(sketch, "E350", {"start": v(-0.2, 15.05) * mm, "end": v(-0.2, 15.12) * mm});
            skLineSegment(sketch, "E351", {"start": v(-0.2, 15.14) * mm, "end": v(-0.2, 15.21) * mm});
            skLineSegment(sketch, "E352", {"start": v(-0.2, 15.21) * mm, "end": v(-0.22, 15.21) * mm});
            skLineSegment(sketch, "E353", {"start": v(-0.22, 15.21) * mm, "end": v(-0.22, 15.14) * mm});
            skLineSegment(sketch, "E354", {"start": v(2.74, -9.8) * mm, "end": v(1.74, -9.8) * mm});
            skLineSegment(sketch, "E355", {"start": v(1.74, -9.8) * mm, "end": v(1.74, -9.7) * mm});
            skLineSegment(sketch, "E356", {"start": v(1.74, -9.7) * mm, "end": v(2.74, -9.7) * mm});
            skLineSegment(sketch, "E357", {"start": v(2.74, -9.7) * mm, "end": v(2.74, -9.8) * mm});
            skLineSegment(sketch, "E358", {"start": v(2.94, -9.64) * mm, "end": v(0.38, -9.64) * mm});
            skLineSegment(sketch, "E359", {"start": v(0.38, -9.64) * mm, "end": v(0.38, -15.8) * mm});
            skLineSegment(sketch, "E360", {"start": v(0.38, -15.8) * mm, "end": v(2.94, -15.8) * mm});
            skLineSegment(sketch, "E361", {"start": v(2.94, -15.8) * mm, "end": v(2.94, -9.64) * mm});
            skLineSegment(sketch, "E362", {"start": v(-2.85, 15.7) * mm, "end": v(-1.85, 15.7) * mm});
            skLineSegment(sketch, "E363", {"start": v(-1.85, 15.7) * mm, "end": v(-1.85, 14.7) * mm});
            skLineSegment(sketch, "E364", {"start": v(-1.85, 14.7) * mm, "end": v(-2.85, 14.7) * mm});
            skLineSegment(sketch, "E365", {"start": v(-2.85, 14.7) * mm, "end": v(-2.85, 15.7) * mm});
            skLineSegment(sketch, "E366", {"start": v(-2.85, 13.5) * mm, "end": v(-1.85, 13.5) * mm});
            skLineSegment(sketch, "E367", {"start": v(-1.85, 13.5) * mm, "end": v(-1.85, 12.5) * mm});
            skLineSegment(sketch, "E368", {"start": v(-1.85, 12.5) * mm, "end": v(-2.85, 12.5) * mm});
            skLineSegment(sketch, "E369", {"start": v(-2.85, 12.5) * mm, "end": v(-2.85, 13.5) * mm});
            skLineSegment(sketch, "E370", {"start": v(2.75, 15.7) * mm, "end": v(1.75, 15.7) * mm});
            skLineSegment(sketch, "E371", {"start": v(1.75, 15.7) * mm, "end": v(1.75, 14.7) * mm});
            skLineSegment(sketch, "E372", {"start": v(1.75, 14.7) * mm, "end": v(2.75, 14.7) * mm});
            skLineSegment(sketch, "E373", {"start": v(2.75, 14.7) * mm, "end": v(2.75, 15.7) * mm});
            skLineSegment(sketch, "E374", {"start": v(2.75, 13.5) * mm, "end": v(1.75, 13.5) * mm});
            skLineSegment(sketch, "E375", {"start": v(1.75, 13.5) * mm, "end": v(1.75, 12.5) * mm});
            skLineSegment(sketch, "E376", {"start": v(1.75, 12.5) * mm, "end": v(2.75, 12.5) * mm});
            skLineSegment(sketch, "E377", {"start": v(2.75, 12.5) * mm, "end": v(2.75, 13.5) * mm});
            skLineSegment(sketch, "E378", {"start": v(-2.7, 13.74) * mm, "end": v(-2, 13.74) * mm});
            skLineSegment(sketch, "E379", {"start": v(-2, 13.74) * mm, "end": v(-2, 14.44) * mm});
            skLineSegment(sketch, "E380", {"start": v(-2, 14.44) * mm, "end": v(-2.7, 14.44) * mm});
            skLineSegment(sketch, "E381", {"start": v(-2.7, 14.44) * mm, "end": v(-2.7, 13.74) * mm});
            skLineSegment(sketch, "E382", {"start": v(2.6, 13.74) * mm, "end": v(1.9, 13.74) * mm});
            skLineSegment(sketch, "E383", {"start": v(1.9, 13.74) * mm, "end": v(1.9, 14.44) * mm});
            skLineSegment(sketch, "E384", {"start": v(1.9, 14.44) * mm, "end": v(2.6, 14.44) * mm});
            skLineSegment(sketch, "E385", {"start": v(2.6, 14.44) * mm, "end": v(2.6, 13.74) * mm});
            skLineSegment(sketch, "E386", {"start": v(2.23, 12.97) * mm, "end": v(2.05, 12.97) * mm});
            skLineSegment(sketch, "E387", {"start": v(2.05, 12.97) * mm, "end": v(2.05, 13.02) * mm});
            skLineSegment(sketch, "E388", {"start": v(2.05, 13.02) * mm, "end": v(2.23, 13.02) * mm});
            skLineSegment(sketch, "E389", {"start": v(2.23, 13.02) * mm, "end": v(2.23, 13.2) * mm});
            skLineSegment(sketch, "E390", {"start": v(2.23, 13.2) * mm, "end": v(2.28, 13.2) * mm});
            skLineSegment(sketch, "E391", {"start": v(2.28, 13.2) * mm, "end": v(2.28, 13.02) * mm});
            skLineSegment(sketch, "E392", {"start": v(2.28, 13.02) * mm, "end": v(2.45, 13.02) * mm});
            skLineSegment(sketch, "E393", {"start": v(2.45, 13.02) * mm, "end": v(2.45, 12.97) * mm});
            skLineSegment(sketch, "E394", {"start": v(2.45, 12.97) * mm, "end": v(2.28, 12.97) * mm});
            skLineSegment(sketch, "E395", {"start": v(2.28, 12.97) * mm, "end": v(2.28, 12.8) * mm});
            skLineSegment(sketch, "E396", {"start": v(2.28, 12.8) * mm, "end": v(2.23, 12.8) * mm});
            skLineSegment(sketch, "E397", {"start": v(2.23, 12.8) * mm, "end": v(2.23, 12.97) * mm});
            skLineSegment(sketch, "E398", {"start": v(2.23, 15.17) * mm, "end": v(2.05, 15.17) * mm});
            skLineSegment(sketch, "E399", {"start": v(2.05, 15.17) * mm, "end": v(2.05, 15.22) * mm});
            skLineSegment(sketch, "E400", {"start": v(2.05, 15.22) * mm, "end": v(2.23, 15.22) * mm});
            skLineSegment(sketch, "E401", {"start": v(2.23, 15.22) * mm, "end": v(2.23, 15.4) * mm});
            skLineSegment(sketch, "E402", {"start": v(2.23, 15.4) * mm, "end": v(2.28, 15.4) * mm});
            skLineSegment(sketch, "E403", {"start": v(2.28, 15.4) * mm, "end": v(2.28, 15.22) * mm});
            skLineSegment(sketch, "E404", {"start": v(2.28, 15.22) * mm, "end": v(2.45, 15.22) * mm});
            skLineSegment(sketch, "E405", {"start": v(2.45, 15.22) * mm, "end": v(2.45, 15.17) * mm});
            skLineSegment(sketch, "E406", {"start": v(2.45, 15.17) * mm, "end": v(2.28, 15.17) * mm});
            skLineSegment(sketch, "E407", {"start": v(2.28, 15.17) * mm, "end": v(2.28, 15) * mm});
            skLineSegment(sketch, "E408", {"start": v(2.28, 15) * mm, "end": v(2.23, 15) * mm});
            skLineSegment(sketch, "E409", {"start": v(2.23, 15) * mm, "end": v(2.23, 15.17) * mm});
            skLineSegment(sketch, "E410", {"start": v(-2.38, 15.17) * mm, "end": v(-2.55, 15.17) * mm});
            skLineSegment(sketch, "E411", {"start": v(-2.55, 15.17) * mm, "end": v(-2.55, 15.22) * mm});
            skLineSegment(sketch, "E412", {"start": v(-2.55, 15.22) * mm, "end": v(-2.38, 15.22) * mm});
            skLineSegment(sketch, "E413", {"start": v(-2.38, 15.22) * mm, "end": v(-2.38, 15.4) * mm});
            skLineSegment(sketch, "E414", {"start": v(-2.38, 15.4) * mm, "end": v(-2.33, 15.4) * mm});
            skLineSegment(sketch, "E415", {"start": v(-2.33, 15.4) * mm, "end": v(-2.33, 15.22) * mm});
            skLineSegment(sketch, "E416", {"start": v(-2.33, 15.22) * mm, "end": v(-2.15, 15.22) * mm});
            skLineSegment(sketch, "E417", {"start": v(-2.15, 15.22) * mm, "end": v(-2.15, 15.17) * mm});
            skLineSegment(sketch, "E418", {"start": v(-2.15, 15.17) * mm, "end": v(-2.33, 15.17) * mm});
            skLineSegment(sketch, "E419", {"start": v(-2.33, 15.17) * mm, "end": v(-2.33, 15) * mm});
            skLineSegment(sketch, "E420", {"start": v(-2.33, 15) * mm, "end": v(-2.38, 15) * mm});
            skLineSegment(sketch, "E421", {"start": v(-2.38, 15) * mm, "end": v(-2.38, 15.17) * mm});
            skLineSegment(sketch, "E422", {"start": v(-2.37, 12.97) * mm, "end": v(-2.55, 12.97) * mm});
            skLineSegment(sketch, "E423", {"start": v(-2.55, 12.97) * mm, "end": v(-2.55, 13.02) * mm});
            skLineSegment(sketch, "E424", {"start": v(-2.55, 13.02) * mm, "end": v(-2.37, 13.02) * mm});
            skLineSegment(sketch, "E425", {"start": v(-2.37, 13.02) * mm, "end": v(-2.37, 13.2) * mm});
            skLineSegment(sketch, "E426", {"start": v(-2.37, 13.2) * mm, "end": v(-2.32, 13.2) * mm});
            skLineSegment(sketch, "E427", {"start": v(-2.32, 13.2) * mm, "end": v(-2.32, 13.02) * mm});
            skLineSegment(sketch, "E428", {"start": v(-2.32, 13.02) * mm, "end": v(-2.15, 13.02) * mm});
            skLineSegment(sketch, "E429", {"start": v(-2.15, 13.02) * mm, "end": v(-2.15, 12.97) * mm});
            skLineSegment(sketch, "E430", {"start": v(-2.15, 12.97) * mm, "end": v(-2.32, 12.97) * mm});
            skLineSegment(sketch, "E431", {"start": v(-2.32, 12.97) * mm, "end": v(-2.32, 12.8) * mm});
            skLineSegment(sketch, "E432", {"start": v(-2.32, 12.8) * mm, "end": v(-2.37, 12.8) * mm});
            skLineSegment(sketch, "E433", {"start": v(-2.37, 12.8) * mm, "end": v(-2.37, 12.97) * mm});
            skLineSegment(sketch, "E434", {"start": v(2.25, 15) * mm, "end": v(2.25, 15.4) * mm});
            skLineSegment(sketch, "E435", {"start": v(2.05, 15.2) * mm, "end": v(2.45, 15.2) * mm});
            skLineSegment(sketch, "E436", {"start": v(0.85, 15) * mm, "end": v(0.85, 15.4) * mm});
            skLineSegment(sketch, "E437", {"start": v(-1.15, 13) * mm, "end": v(-0.75, 13) * mm});
            skLineSegment(sketch, "E438", {"start": v(-0.95, 15) * mm, "end": v(-0.95, 15.4) * mm});
            skLineSegment(sketch, "E439", {"start": v(-1.15, 15.2) * mm, "end": v(-0.75, 15.2) * mm});
            skLineSegment(sketch, "E440", {"start": v(-2.35, 15) * mm, "end": v(-2.35, 15.4) * mm});
            skLineSegment(sketch, "E441", {"start": v(-2.55, 15.2) * mm, "end": v(-2.15, 15.2) * mm});
            skLineSegment(sketch, "E442", {"start": v(-2.35, 12.8) * mm, "end": v(-2.35, 13.2) * mm});
            skLineSegment(sketch, "E443", {"start": v(-2.55, 13) * mm, "end": v(-2.15, 13) * mm});
            skCircle(sketch, "E444", {"center": v(1.55, 10.3) * mm, "radius": 0.25 * mm});
            skCircle(sketch, "E445", {"center": v(-1.65, 10.3) * mm, "radius": 0.25 * mm});
            skCircle(sketch, "E446", {"center": v(1.55, 5.3) * mm, "radius": 0.25 * mm});
            skCircle(sketch, "E447", {"center": v(-1.65, 5.3) * mm, "radius": 0.25 * mm});
            skCircle(sketch, "E448", {"center": v(1.55, -0.7) * mm, "radius": 0.25 * mm});
            skCircle(sketch, "E449", {"center": v(-1.65, -0.7) * mm, "radius": 0.25 * mm});
            skCircle(sketch, "E450", {"center": v(1.55, -6.7) * mm, "radius": 0.25 * mm});
            skCircle(sketch, "E451", {"center": v(-1.65, -6.7) * mm, "radius": 0.25 * mm});
            skSolve(sketch);
        }
        {
            var Q0;
            Q0=qCreatedBy(makeId("Top.planeOp"),FACE);
            var sketch = newSketch(context, id + "F1", { "sketchPlane" : qUnion([Q0])});
            skCircle(sketch, "E452.0", {"center": v(-1.65, 14.9) * mm, "radius": 0.25 * mm});
            skCircle(sketch, "E453.0", {"center": v(1.55, 14.9) * mm, "radius": 0.25 * mm});
            skCircle(sketch, "E454.0", {"center": v(1.55, 13.3) * mm, "radius": 0.25 * mm});
            skCircle(sketch, "E455.0", {"center": v(-1.65, 13.3) * mm, "radius": 0.25 * mm});
            skCircle(sketch, "E456.0", {"center": v(1.55, 10.3) * mm, "radius": 0.25 * mm});
            skCircle(sketch, "E457.0", {"center": v(-1.65, 10.3) * mm, "radius": 0.25 * mm});
            skCircle(sketch, "E458.0", {"center": v(1.55, 5.3) * mm, "radius": 0.25 * mm});
            skCircle(sketch, "E459.0", {"center": v(-1.65, 5.3) * mm, "radius": 0.25 * mm});
            skCircle(sketch, "E459.1", {"center": v(-1.65, -0.7) * mm, "radius": 0.25 * mm});
            skCircle(sketch, "E459.2", {"center": v(1.55, -0.7) * mm, "radius": 0.25 * mm});
            skSolve(sketch);
        }
        {
            var Q0;
            Q0=qCreatedBy(makeId("Top.planeOp"),FACE);
            var sketch = newSketch(context, id + "F2", { "sketchPlane" : qUnion([Q0])});
            skLineSegment(sketch, "E460.bottom", {"start": v(-30, 30) * mm, "end": v(30, 30) * mm});
            skLineSegment(sketch, "E460.top", {"start": v(-30, -30) * mm, "end": v(30, -30) * mm});
            skLineSegment(sketch, "E460.left", {"start": v(-30, 30) * mm, "end": v(-30, -30) * mm});
            skLineSegment(sketch, "E460.right", {"start": v(30, 30) * mm, "end": v(30, -30) * mm});
            skSolve(sketch);
        }
        {
            var Q0;
            Q0 = qSketchRegion(id + "F2", true);
            extrude(context, id + "F3", {"entities" : qUnion([Q0]), "oppositeDirection" : true, "depth" : 5 * mm, "offsetDistance" : 25 * mm});
        }
        {
            var Q0;
            Q0=makeQuery(id+"F3.opExtrude","CAP_FACE",FACE,{"disambiguationData":[OSD([sQuery(id+"F2.wireOp",EDGE,"E460.bottom"),sQuery(id+"F2.wireOp",EDGE,"E460.top"),sQuery(id+"F2.wireOp",EDGE,"E460.left"),sQuery(id+"F2.wireOp",EDGE,"E460.right")])],"isStart":true});
            var sketch = newSketch(context, id + "F4", { "sketchPlane" : qUnion([Q0])});
            skLineSegment(sketch, "E461.0", {"start": v(-28, 28) * mm, "end": v(-28, -28) * mm});
            skLineSegment(sketch, "E461.1", {"start": v(28, 28) * mm, "end": v(-28, 28) * mm});
            skLineSegment(sketch, "E461.2", {"start": v(28, -28) * mm, "end": v(28, 28) * mm});
            skLineSegment(sketch, "E461.3", {"start": v(-28, -28) * mm, "end": v(28, -28) * mm});
            skSolve(sketch);
        }
        {
            var Q0;
            Q0=makeQuery(id+"F4.imprint","IMPRINT",FACE,{"disambiguationData":[TD([[makeQuery(id+"F4.imprint","IMPRINT",EDGE,{"derivedFrom":sQuery(id+"F4.wireOp",EDGE,"E461.0")}),-1.0]])]});
            extrude(context, id + "F5", {"entities" : qUnion([Q0]), "operationType" : NewBodyOperationType.REMOVE, "oppositeDirection" : true, "depth" : 1 * mm, "offsetDistance" : 25 * mm});
        }
        {
            var Q0;
            Q0 = qSketchRegion(id + "F1", true);
            extrude(context, id + "F6", {"entities" : qUnion([Q0]), "operationType" : NewBodyOperationType.ADD, "depth" : 0.5 * mm, "offsetDistance" : 25 * mm});
        }
        {
            var Q0;
            Q0=makeQuery(id+"F3.opExtrude","CAP_FACE",FACE,{"disambiguationData":[OSD([sQuery(id+"F2.wireOp",EDGE,"E460.bottom"),sQuery(id+"F2.wireOp",EDGE,"E460.top"),sQuery(id+"F2.wireOp",EDGE,"E460.left"),sQuery(id+"F2.wireOp",EDGE,"E460.right")])],"isStart":true});
            var sketch = newSketch(context, id + "F7", { "sketchPlane" : qUnion([Q0])});
            skCircle(sketch, "E462", {"center": v(25, 25) * mm, "radius": 1 * mm});
            skCircle(sketch, "E463.MirrorC", {"center": v(25, -25) * mm, "radius": 1 * mm});
            skCircle(sketch, "E464.MirrorC", {"center": v(-25, -25) * mm, "radius": 1 * mm});
            skCircle(sketch, "E465.MirrorC", {"center": v(-25, 25) * mm, "radius": 1 * mm});
            skSolve(sketch);
        }
        {
            var Q0;
            Q0=makeQuery(id+"F7.imprint","IMPRINT",FACE,{"disambiguationData":[TD([[makeQuery(id+"F7.imprint","IMPRINT",EDGE,{"derivedFrom":sQuery(id+"F7.wireOp",EDGE,"E463.MirrorC")}),-1.0]])]});
            var Q1;
            Q1=makeQuery(id+"F7.imprint","IMPRINT",FACE,{"disambiguationData":[TD([[makeQuery(id+"F7.imprint","IMPRINT",EDGE,{"derivedFrom":sQuery(id+"F7.wireOp",EDGE,"E464.MirrorC")}),1.0]])]});
            var Q2;
            Q2=makeQuery(id+"F7.imprint","IMPRINT",FACE,{"disambiguationData":[TD([[makeQuery(id+"F7.imprint","IMPRINT",EDGE,{"derivedFrom":sQuery(id+"F7.wireOp",EDGE,"E465.MirrorC")}),-1.0]])]});
            var Q3;
            Q3=makeQuery(id+"F7.imprint","IMPRINT",FACE,{"disambiguationData":[TD([[makeQuery(id+"F7.imprint","IMPRINT",EDGE,{"derivedFrom":sQuery(id+"F7.wireOp",EDGE,"E462")}),1.0]])]});
            extrude(context, id + "F8", {"entities" : qUnion([Q0, Q1, Q2, Q3]), "operationType" : NewBodyOperationType.ADD, "depth" : 3 * mm, "offsetDistance" : 25 * mm});
        }
        {
            var Q0;
            Q0=qCreatedBy(makeId("Top.planeOp"),FACE);
            cPlane(context, id + "F9", {"entities" : qUnion([Q0]), "cplaneType" : CPlaneType.OFFSET, "offset" : 25 * mm, "width" : 150 * mm, "height" : 150 * mm});
        }
        {
            var Q0;
            Q0=qCreatedBy(id+"F9.planeOp",FACE);
            var sketch = newSketch(context, id + "F10", { "sketchPlane" : qUnion([Q0])});
            skLineSegment(sketch, "E466.0.0", {"start": v(30, 30) * mm, "end": v(-30, 30) * mm});
            skLineSegment(sketch, "E466.0.1", {"start": v(-30, 30) * mm, "end": v(-30, -30) * mm});
            skLineSegment(sketch, "E466.0.2", {"start": v(-30, -30) * mm, "end": v(30, -30) * mm});
            skLineSegment(sketch, "E466.0.3", {"start": v(30, -30) * mm, "end": v(30, 30) * mm});
            skLineSegment(sketch, "E467.0.0", {"start": v(-28, 28) * mm, "end": v(-28, -28) * mm});
            skLineSegment(sketch, "E467.0.1", {"start": v(-28, -28) * mm, "end": v(28, -28) * mm});
            skLineSegment(sketch, "E467.0.2", {"start": v(28, -28) * mm, "end": v(28, 28) * mm});
            skLineSegment(sketch, "E467.0.3", {"start": v(28, 28) * mm, "end": v(-28, 28) * mm});
            skCircle(sketch, "E468.0", {"center": v(-25, 25) * mm, "radius": 1 * mm});
            skCircle(sketch, "E469.0", {"center": v(25, 25) * mm, "radius": 1 * mm});
            skCircle(sketch, "E470.0", {"center": v(25, -25) * mm, "radius": 1 * mm});
            skCircle(sketch, "E471.0", {"center": v(-25, -25) * mm, "radius": 1 * mm});
            skCircle(sketch, "E472.0", {"center": v(25, 25) * mm, "radius": 1.1 * mm});
            skCircle(sketch, "E473.0", {"center": v(-25, 25) * mm, "radius": 1.1 * mm});
            skCircle(sketch, "E474.0", {"center": v(-25, -25) * mm, "radius": 1.1 * mm});
            skCircle(sketch, "E475.0", {"center": v(25, -25) * mm, "radius": 1.1 * mm});
            skSolve(sketch);
        }
        {
            var Q0;
            Q0=makeQuery(id+"F10.imprint","IMPRINT",FACE,{"disambiguationData":[TD([[makeQuery(id+"F10.imprint","IMPRINT",EDGE,{"derivedFrom":sQuery(id+"F10.wireOp",EDGE,"E466.0.0")}),1.0]])]});
            var Q1;
            Q1=makeQuery(id+"F10.imprint","IMPRINT",FACE,{"disambiguationData":[TD([[makeQuery(id+"F10.imprint","IMPRINT",EDGE,{"derivedFrom":sQuery(id+"F10.wireOp",EDGE,"E467.0.0")}),1.0]])]});
            var Q2;
            Q2=sQuery(id+"F10.wireOp",EDGE,"E466.0.2");
            var Q3;
            Q3=sQuery(id+"F10.wireOp",EDGE,"E466.0.1");
            var Q4;
            Q4=sQuery(id+"F10.wireOp",EDGE,"E466.0.3");
            var Q5;
            Q5=sQuery(id+"F10.wireOp",EDGE,"E466.0.0");
            extrude(context, id + "F11", {"entities" : qUnion([Q0, Q1]), "surfaceEntities" : qUnion([Q2, Q3, Q4, Q5]), "depth" : 5 * mm, "offsetDistance" : 25 * mm});
        }
        {
            var Q0;
            Q0=qCreatedBy(id+"F9.planeOp",FACE);
            var sketch = newSketch(context, id + "F12", { "sketchPlane" : qUnion([Q0])});
            skCircle(sketch, "E476.0", {"center": v(-1.65, 14.9) * mm, "radius": 0.25 * mm});
            skLineSegment(sketch, "E477.0.0", {"start": v(-30, -30) * mm, "end": v(30, -30) * mm});
            skLineSegment(sketch, "E477.0.1", {"start": v(30, -30) * mm, "end": v(30, 30) * mm});
            skLineSegment(sketch, "E477.0.2", {"start": v(30, 30) * mm, "end": v(-30, 30) * mm});
            skLineSegment(sketch, "E477.0.3", {"start": v(-30, 30) * mm, "end": v(-30, -30) * mm});
            skCircle(sketch, "E478.0", {"center": v(1.55, 14.9) * mm, "radius": 0.25 * mm});
            skCircle(sketch, "E479.0", {"center": v(1.55, 13.3) * mm, "radius": 0.25 * mm});
            skCircle(sketch, "E480.0", {"center": v(-1.65, 13.3) * mm, "radius": 0.25 * mm});
            skCircle(sketch, "E481.0", {"center": v(-1.65, 10.3) * mm, "radius": 0.25 * mm});
            skCircle(sketch, "E482.0", {"center": v(1.55, 10.3) * mm, "radius": 0.25 * mm});
            skCircle(sketch, "E483.0", {"center": v(1.55, -0.7) * mm, "radius": 0.25 * mm});
            skCircle(sketch, "E484.0", {"center": v(-1.65, -0.7) * mm, "radius": 0.25 * mm});
            skCircle(sketch, "E485.0", {"center": v(-1.65, 5.3) * mm, "radius": 0.25 * mm});
            skCircle(sketch, "E486.0", {"center": v(1.55, 5.3) * mm, "radius": 0.25 * mm});
            skCircle(sketch, "E487.0", {"center": v(-1.65, 10.3) * mm, "radius": 0.35 * mm});
            skCircle(sketch, "E488.0", {"center": v(1.55, 10.3) * mm, "radius": 0.35 * mm});
            skCircle(sketch, "E489.0", {"center": v(-1.65, 13.3) * mm, "radius": 0.35 * mm});
            skCircle(sketch, "E490.0", {"center": v(1.55, 13.3) * mm, "radius": 0.35 * mm});
            skCircle(sketch, "E491.0", {"center": v(1.55, 14.9) * mm, "radius": 0.35 * mm});
            skCircle(sketch, "E492.0", {"center": v(-1.65, 14.9) * mm, "radius": 0.35 * mm});
            skCircle(sketch, "E493.0", {"center": v(1.55, 5.3) * mm, "radius": 0.35 * mm});
            skCircle(sketch, "E494.0", {"center": v(-1.65, 5.3) * mm, "radius": 0.35 * mm});
            skCircle(sketch, "E495.0", {"center": v(1.55, -0.7) * mm, "radius": 0.35 * mm});
            skCircle(sketch, "E496.0", {"center": v(-1.65, -0.7) * mm, "radius": 0.35 * mm});
            skSolve(sketch);
        }
        {
            var Q0;
            Q0=makeQuery(id+"F12.imprint","IMPRINT",FACE,{"disambiguationData":[TD([[makeQuery(id+"F12.imprint","IMPRINT",EDGE,{"derivedFrom":sQuery(id+"F12.wireOp",EDGE,"E484.0")}),-1.0]])]});
            var Q1;
            Q1=makeQuery(id+"F12.imprint","IMPRINT",FACE,{"disambiguationData":[TD([[makeQuery(id+"F12.imprint","IMPRINT",EDGE,{"derivedFrom":sQuery(id+"F12.wireOp",EDGE,"E484.0")}),1.0]])]});
            var Q2;
            Q2=makeQuery(id+"F12.imprint","IMPRINT",FACE,{"disambiguationData":[TD([[makeQuery(id+"F12.imprint","IMPRINT",EDGE,{"derivedFrom":sQuery(id+"F12.wireOp",EDGE,"E483.0")}),1.0]])]});
            var Q3;
            Q3=makeQuery(id+"F12.imprint","IMPRINT",FACE,{"disambiguationData":[TD([[makeQuery(id+"F12.imprint","IMPRINT",EDGE,{"derivedFrom":sQuery(id+"F12.wireOp",EDGE,"E483.0")}),-1.0]])]});
            var Q4;
            Q4=makeQuery(id+"F12.imprint","IMPRINT",FACE,{"disambiguationData":[TD([[makeQuery(id+"F12.imprint","IMPRINT",EDGE,{"derivedFrom":sQuery(id+"F12.wireOp",EDGE,"E486.0")}),1.0]])]});
            var Q5;
            Q5=makeQuery(id+"F12.imprint","IMPRINT",FACE,{"disambiguationData":[TD([[makeQuery(id+"F12.imprint","IMPRINT",EDGE,{"derivedFrom":sQuery(id+"F12.wireOp",EDGE,"E486.0")}),-1.0]])]});
            var Q6;
            Q6=makeQuery(id+"F12.imprint","IMPRINT",FACE,{"disambiguationData":[TD([[makeQuery(id+"F12.imprint","IMPRINT",EDGE,{"derivedFrom":sQuery(id+"F12.wireOp",EDGE,"E485.0")}),1.0]])]});
            var Q7;
            Q7=makeQuery(id+"F12.imprint","IMPRINT",FACE,{"disambiguationData":[TD([[makeQuery(id+"F12.imprint","IMPRINT",EDGE,{"derivedFrom":sQuery(id+"F12.wireOp",EDGE,"E485.0")}),-1.0]])]});
            var Q8;
            Q8=makeQuery(id+"F12.imprint","IMPRINT",FACE,{"disambiguationData":[TD([[makeQuery(id+"F12.imprint","IMPRINT",EDGE,{"derivedFrom":sQuery(id+"F12.wireOp",EDGE,"E481.0")}),-1.0]])]});
            var Q9;
            Q9=makeQuery(id+"F12.imprint","IMPRINT",FACE,{"disambiguationData":[TD([[makeQuery(id+"F12.imprint","IMPRINT",EDGE,{"derivedFrom":sQuery(id+"F12.wireOp",EDGE,"E481.0")}),1.0]])]});
            var Q10;
            Q10=makeQuery(id+"F12.imprint","IMPRINT",FACE,{"disambiguationData":[TD([[makeQuery(id+"F12.imprint","IMPRINT",EDGE,{"derivedFrom":sQuery(id+"F12.wireOp",EDGE,"E482.0")}),1.0]])]});
            var Q11;
            Q11=makeQuery(id+"F12.imprint","IMPRINT",FACE,{"disambiguationData":[TD([[makeQuery(id+"F12.imprint","IMPRINT",EDGE,{"derivedFrom":sQuery(id+"F12.wireOp",EDGE,"E482.0")}),-1.0]])]});
            var Q12;
            Q12=makeQuery(id+"F12.imprint","IMPRINT",FACE,{"disambiguationData":[TD([[makeQuery(id+"F12.imprint","IMPRINT",EDGE,{"derivedFrom":sQuery(id+"F12.wireOp",EDGE,"E476.0")}),1.0]])]});
            var Q13;
            Q13=makeQuery(id+"F12.imprint","IMPRINT",FACE,{"disambiguationData":[TD([[makeQuery(id+"F12.imprint","IMPRINT",EDGE,{"derivedFrom":sQuery(id+"F12.wireOp",EDGE,"E476.0")}),-1.0]])]});
            var Q14;
            Q14=makeQuery(id+"F12.imprint","IMPRINT",FACE,{"disambiguationData":[TD([[makeQuery(id+"F12.imprint","IMPRINT",EDGE,{"derivedFrom":sQuery(id+"F12.wireOp",EDGE,"E480.0")}),1.0]])]});
            var Q15;
            Q15=makeQuery(id+"F12.imprint","IMPRINT",FACE,{"disambiguationData":[TD([[makeQuery(id+"F12.imprint","IMPRINT",EDGE,{"derivedFrom":sQuery(id+"F12.wireOp",EDGE,"E480.0")}),-1.0]])]});
            var Q16;
            Q16=makeQuery(id+"F12.imprint","IMPRINT",FACE,{"disambiguationData":[TD([[makeQuery(id+"F12.imprint","IMPRINT",EDGE,{"derivedFrom":sQuery(id+"F12.wireOp",EDGE,"E479.0")}),1.0]])]});
            var Q17;
            Q17=makeQuery(id+"F12.imprint","IMPRINT",FACE,{"disambiguationData":[TD([[makeQuery(id+"F12.imprint","IMPRINT",EDGE,{"derivedFrom":sQuery(id+"F12.wireOp",EDGE,"E479.0")}),-1.0]])]});
            var Q18;
            Q18=makeQuery(id+"F12.imprint","IMPRINT",FACE,{"disambiguationData":[TD([[makeQuery(id+"F12.imprint","IMPRINT",EDGE,{"derivedFrom":sQuery(id+"F12.wireOp",EDGE,"E478.0")}),1.0]])]});
            var Q19;
            Q19=makeQuery(id+"F12.imprint","IMPRINT",FACE,{"disambiguationData":[TD([[makeQuery(id+"F12.imprint","IMPRINT",EDGE,{"derivedFrom":sQuery(id+"F12.wireOp",EDGE,"E478.0")}),-1.0]])]});
            extrude(context, id + "F13", {"entities" : qUnion([Q0, Q1, Q2, Q3, Q4, Q5, Q6, Q7, Q8, Q9, Q10, Q11, Q12, Q13, Q14, Q15, Q16, Q17, Q18, Q19]), "operationType" : NewBodyOperationType.REMOVE, "depth" : 0.7 * mm, "offsetDistance" : 25 * mm});
        }
        {
            var Q0;
            Q0=makeQuery(id+"F10.imprint","IMPRINT",FACE,{"disambiguationData":[TD([[makeQuery(id+"F10.imprint","IMPRINT",EDGE,{"derivedFrom":sQuery(id+"F10.wireOp",EDGE,"E466.0.0")}),1.0]])]});
            extrude(context, id + "F14", {"entities" : qUnion([Q0]), "operationType" : NewBodyOperationType.REMOVE, "depth" : 1 * mm, "offsetDistance" : 25 * mm});
        }
    });
